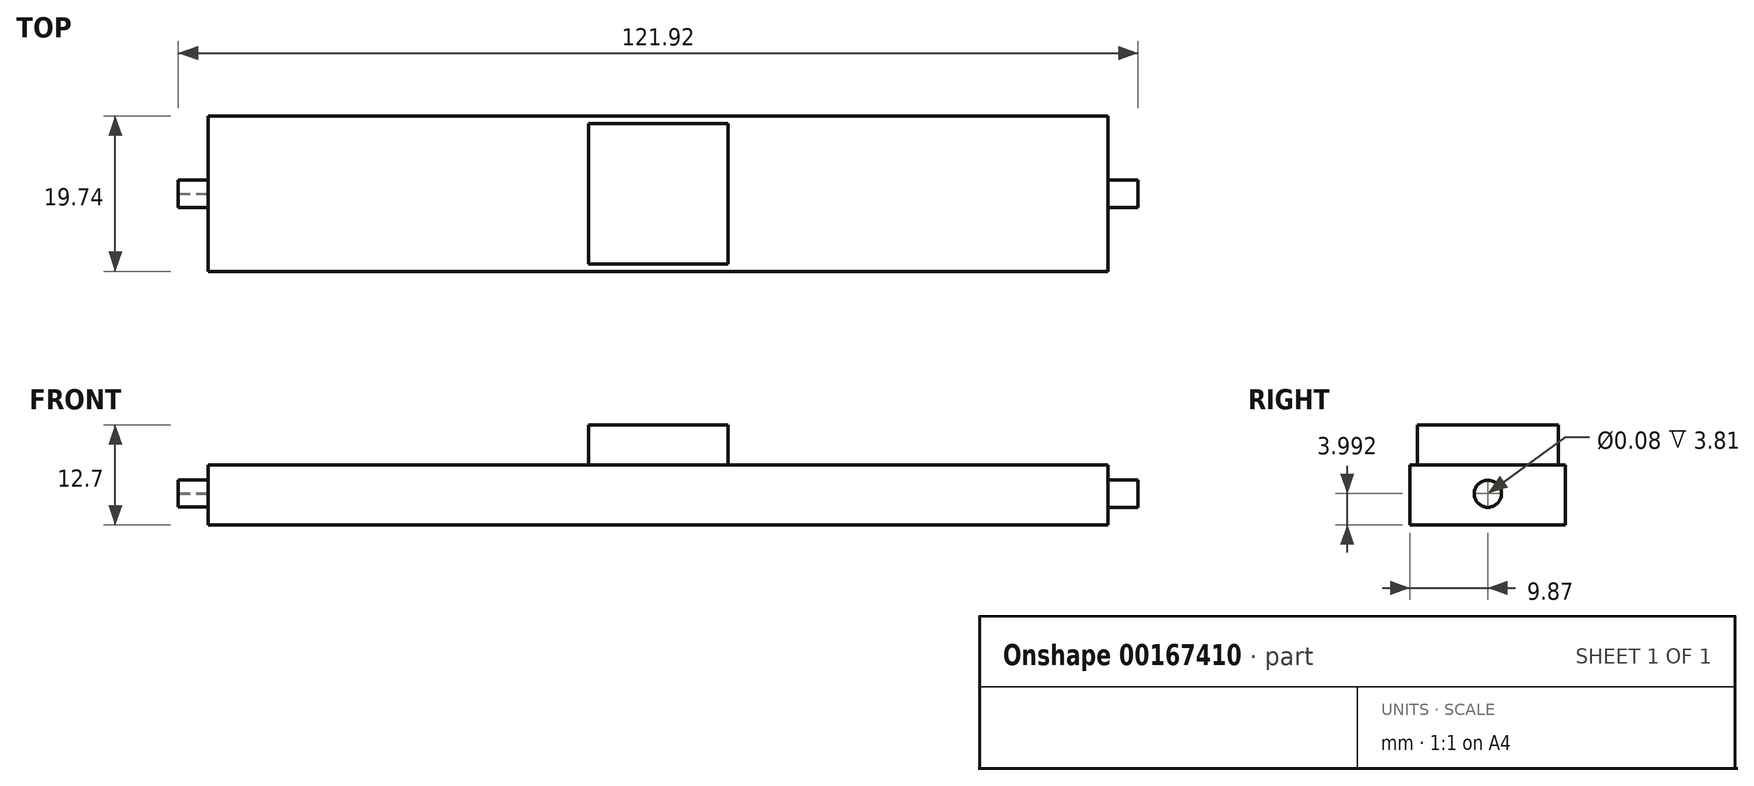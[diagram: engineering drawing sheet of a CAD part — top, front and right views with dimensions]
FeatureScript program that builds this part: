
annotation { "Feature Type Name" : "Feature", "Feature Type Description" : "" }
export const myFeature = defineFeature(function(context is Context, id is Id, definition is map)
    precondition{}
    {
        {
            var Q0;
            Q0=qCreatedBy(makeId("Top.planeOp"),FACE);
            var sketch = newSketch(context, id + "F0", { "sketchPlane" : qUnion([Q0])});
            skLineSegment(sketch, "E0.bottom", {"start": v(8.87, -8.92) * mm, "end": v(-8.87, -8.92) * mm});
            skLineSegment(sketch, "E0.top", {"start": v(8.87, 8.92) * mm, "end": v(-8.87, 8.92) * mm});
            skLineSegment(sketch, "E0.left", {"start": v(8.87, -8.92) * mm, "end": v(8.87, 8.92) * mm});
            skLineSegment(sketch, "E0.right", {"start": v(-8.87, -8.92) * mm, "end": v(-8.87, 8.92) * mm});
            skPoint(sketch, "E0.middle", {"position": v(0, 0) * mm});
            skSolve(sketch);
        }
        {
            var Q0;
            Q0 = qSketchRegion(id + "F0", true);
            extrude(context, id + "F1", {"entities" : qUnion([Q0]), "depth" : 5.08 * mm});
        }
        {
            var Q0;
            Q0=qCreatedBy(makeId("Top.planeOp"),FACE);
            var sketch = newSketch(context, id + "F2", { "sketchPlane" : qUnion([Q0])});
            skLineSegment(sketch, "E1.bottom", {"start": v(57.15, -9.87) * mm, "end": v(-57.15, -9.87) * mm});
            skLineSegment(sketch, "E1.top", {"start": v(57.15, 9.87) * mm, "end": v(-57.15, 9.87) * mm});
            skLineSegment(sketch, "E1.left", {"start": v(57.15, -9.87) * mm, "end": v(57.15, 9.87) * mm});
            skLineSegment(sketch, "E1.right", {"start": v(-57.15, -9.87) * mm, "end": v(-57.15, 9.87) * mm});
            skPoint(sketch, "E1.middle", {"position": v(0, 0) * mm});
            skSolve(sketch);
        }
        {
            var Q0;
            Q0 = qSketchRegion(id + "F2", true);
            extrude(context, id + "F3", {"entities" : qUnion([Q0]), "operationType" : NewBodyOperationType.ADD, "oppositeDirection" : true, "depth" : 7.62 * mm});
        }
        {
            var Q0;
            Q0=makeQuery(id+"F3.opExtrude","SWEPT_FACE",FACE,{"disambiguationData":[OSD([sQuery(id+"F2.wireOp",EDGE,"E1.left")])]});
            var sketch = newSketch(context, id + "F4", { "sketchPlane" : qUnion([Q0])});
            skCircle(sketch, "E2", {"center": v(0, -3.66) * mm, "radius": 1.72 * mm});
            skPoint(sketch, "E2.centerSnap0", {"position": v(0, -7.62) * mm});
            skSolve(sketch);
        }
        {
            var Q0;
            Q0=makeQuery(id+"F3.opExtrude","SWEPT_FACE",FACE,{"disambiguationData":[OSD([sQuery(id+"F2.wireOp",EDGE,"E1.right")])]});
            var sketch = newSketch(context, id + "F5", { "sketchPlane" : qUnion([Q0])});
            skCircle(sketch, "E3", {"center": v(0, -3.63) * mm, "radius": 0.04 * mm});
            skCircle(sketch, "E4", {"center": v(0, -3.63) * mm, "radius": 1.72 * mm});
            skSolve(sketch);
        }
        {
            var Q0;
            Q0 = qSketchRegion(id + "F5", true);
            var Q1;
            Q1 = qSketchRegion(id + "F4", true);
            extrude(context, id + "F6", {"entities" : qUnion([Q0, Q1]), "operationType" : NewBodyOperationType.ADD, "endBound" : BoundingType.SYMMETRIC, "depth" : 7.62 * mm});
        }
    });
